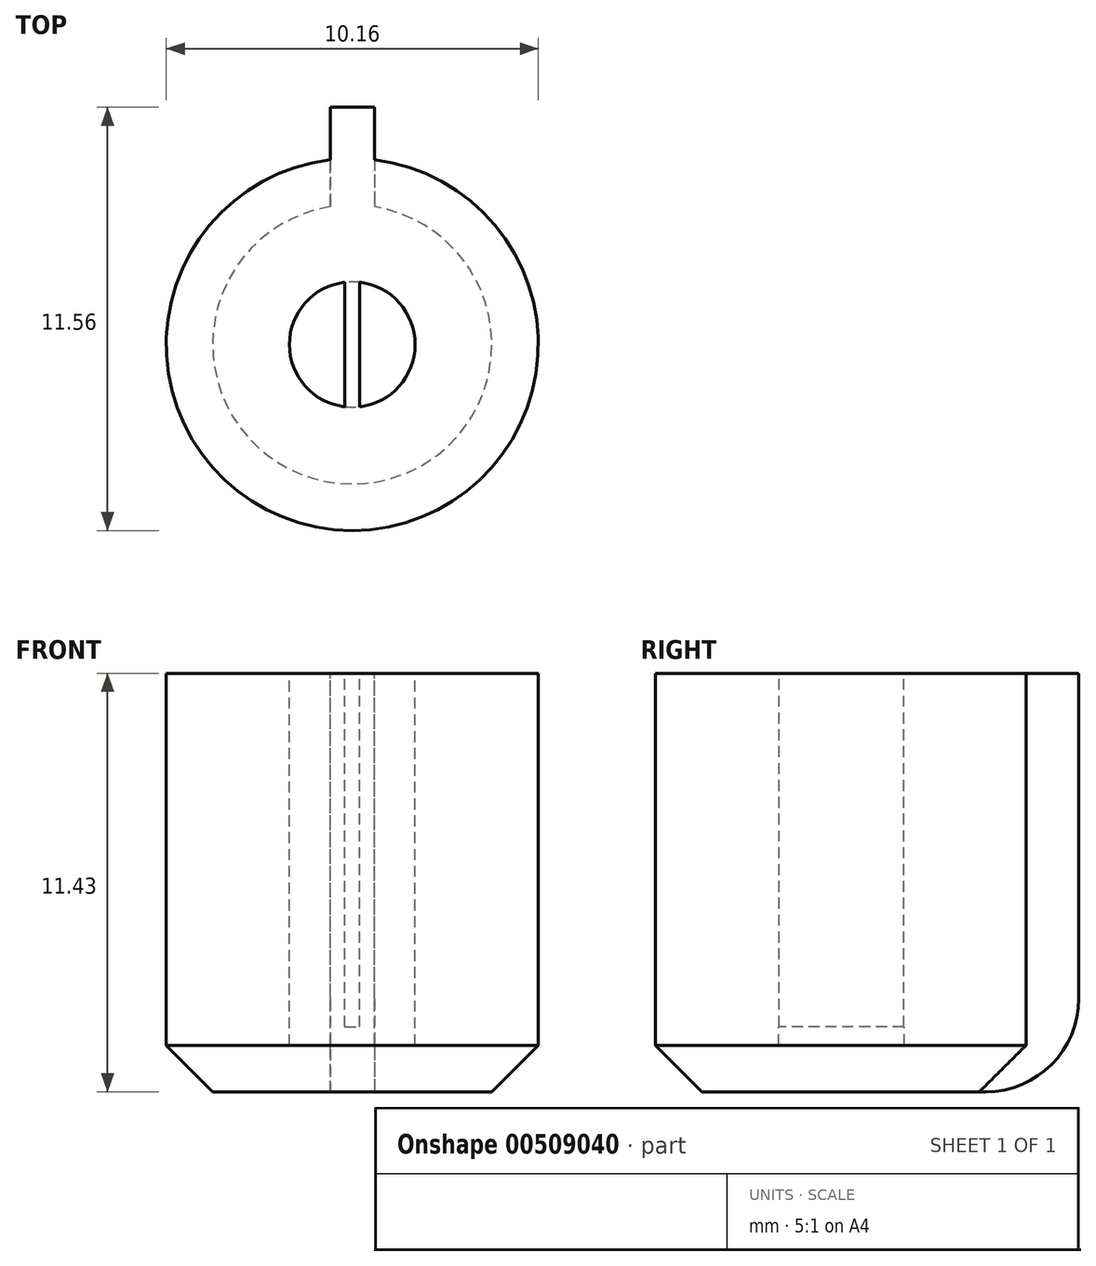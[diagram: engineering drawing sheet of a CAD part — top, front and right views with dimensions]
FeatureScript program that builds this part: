
annotation { "Feature Type Name" : "Feature", "Feature Type Description" : "" }
export const myFeature = defineFeature(function(context is Context, id is Id, definition is map)
    precondition{}
    {
        {
            var Q0;
            Q0=qCreatedBy(makeId("Top.planeOp"),FACE);
            var sketch = newSketch(context, id + "F0", { "sketchPlane" : qUnion([Q0])});
            skCircle(sketch, "E0", {"center": v(0, 0) * mm, "radius": 5.08 * mm});
            skLineSegment(sketch, "E1.bottom", {"start": v(0.6, 6.48) * mm, "end": v(-0.6, 6.48) * mm});
            skLineSegment(sketch, "E1.top", {"start": v(0.6, 3.68) * mm, "end": v(-0.6, 3.68) * mm});
            skLineSegment(sketch, "E1.left", {"start": v(0.6, 6.48) * mm, "end": v(0.6, 3.68) * mm});
            skLineSegment(sketch, "E1.right", {"start": v(-0.6, 6.48) * mm, "end": v(-0.6, 3.68) * mm});
            skPoint(sketch, "E1.middle", {"position": v(0, 5.08) * mm});
            skSolve(sketch);
        }
        {
            var Q0;
            Q0=qSketchRegion(id+"F0",true);
            extrude(context, id + "F1", {"entities" : qUnion([Q0]), "oppositeDirection" : true, "depth" : 11.43 * mm});
        }
        {
            var Q0;
            Q0=makeQuery(id+"F1.opExtrude","CAP_FACE",FACE,{"disambiguationData":[OSD([sQuery(id+"F0.wireOp",EDGE,"E0")])],"isStart":true});
            var sketch = newSketch(context, id + "F2", { "sketchPlane" : qUnion([Q0])});
            skCircle(sketch, "E2", {"center": v(0, 0) * mm, "radius": 1.71 * mm});
            skSolve(sketch);
        }
        {
            var Q0;
            Q0=qSketchRegion(id+"F2",true);
            extrude(context, id + "F3", {"entities" : qUnion([Q0]), "operationType" : NewBodyOperationType.REMOVE, "oppositeDirection" : true, "depth" : 10.16 * mm});
        }
        {
            var Q0;
            Q0=qCreatedBy(makeId("Top.planeOp"),FACE);
            var sketch = newSketch(context, id + "F4", { "sketchPlane" : qUnion([Q0])});
            skLineSegment(sketch, "E3.bottom", {"start": v(0.2, 2.58) * mm, "end": v(-0.2, 2.58) * mm});
            skLineSegment(sketch, "E3.top", {"start": v(0.2, -2.58) * mm, "end": v(-0.2, -2.58) * mm});
            skLineSegment(sketch, "E3.left", {"start": v(0.2, 2.58) * mm, "end": v(0.2, -2.58) * mm});
            skLineSegment(sketch, "E3.right", {"start": v(-0.2, 2.58) * mm, "end": v(-0.2, -2.58) * mm});
            skPoint(sketch, "E3.middle", {"position": v(0, 0) * mm});
            skSolve(sketch);
        }
        {
            var Q0;
            Q0=qSketchRegion(id+"F4",true);
            extrude(context, id + "F5", {"entities" : qUnion([Q0]), "operationType" : NewBodyOperationType.ADD, "oppositeDirection" : true, "depth" : 9.65 * mm});
        }
        {
            var Q0;
            Q0=makeQuery(id+"F1.opExtrude","CAP_EDGE",EDGE,{"disambiguationData":[OSD([sQuery(id+"F0.wireOp",EDGE,"E0")])],"isStart":false});
            chamfer(context, id + "F6", {"entities" : qUnion([Q0]), "width" : 1.27 * mm, "tangentPropagation" : true});
        }
        {
            var Q0;
            Q0=makeQuery(id+"F1.opExtrude","CAP_EDGE",EDGE,{"disambiguationData":[OSD([sQuery(id+"F0.wireOp",EDGE,"E1.bottom")])],"isStart":false});
            fillet(context, id + "F7", {"entities" : qUnion([Q0]), "radius" : 2.54 * mm, "tangentPropagation" : true, "allowEdgeOverflow" : false});
        }
    });
